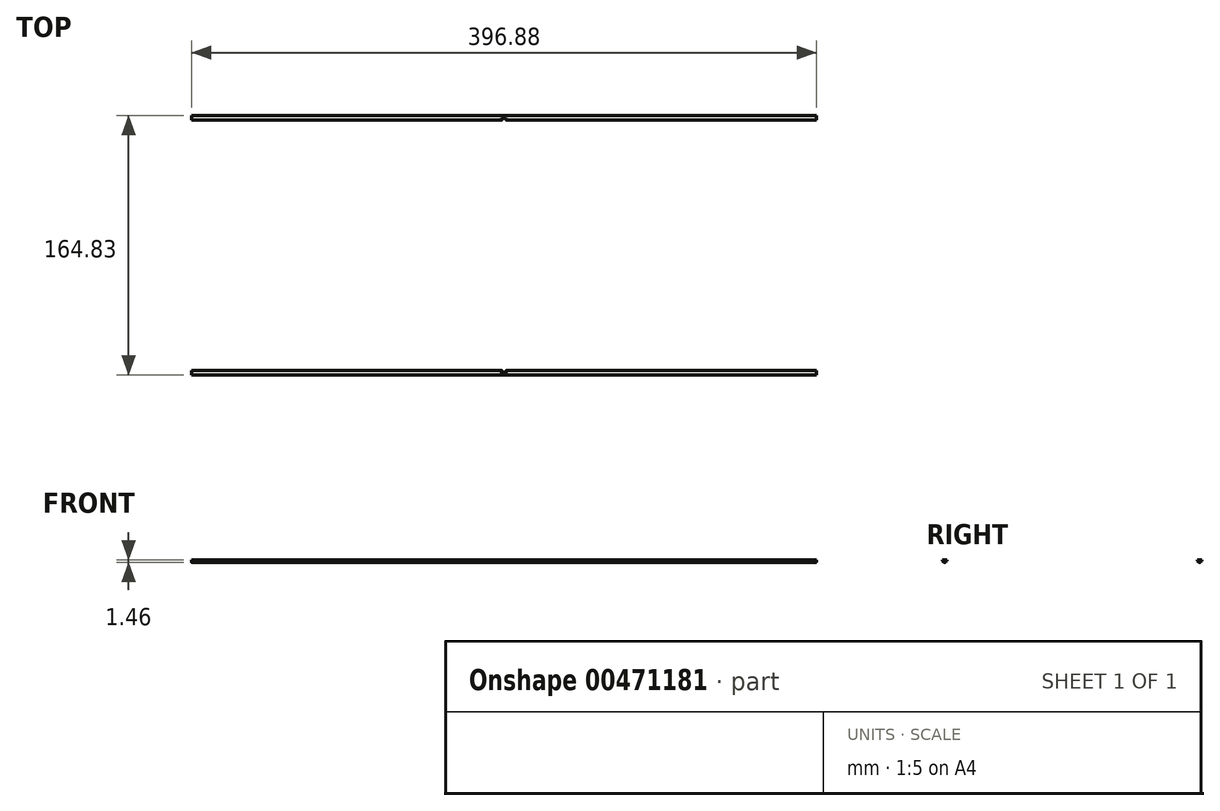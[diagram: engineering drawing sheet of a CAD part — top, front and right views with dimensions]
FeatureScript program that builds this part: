
annotation { "Feature Type Name" : "Feature", "Feature Type Description" : "" }
export const myFeature = defineFeature(function(context is Context, id is Id, definition is map)
    precondition{}
    {
        {
            var Q0;
            Q0=qCreatedBy(makeId("Top.planeOp"),FACE);
            var sketch = newSketch(context, id + "F0", { "sketchPlane" : qUnion([Q0])});
            skLineSegment(sketch, "E0", {"start": v(0, 0) * mm, "end": v(396.88, 0) * mm});
            skLineSegment(sketch, "E1", {"start": v(396.88, 0) * mm, "end": v(396.88, -193.68) * mm});
            skLineSegment(sketch, "E2", {"start": v(396.88, -193.68) * mm, "end": v(0, -193.68) * mm});
            skLineSegment(sketch, "E3", {"start": v(0, -193.68) * mm, "end": v(0, 0) * mm});
            skLineSegment(sketch, "E4.0", {"start": v(50.8, -31.75) * mm, "end": v(166.69, -31.75) * mm});
            skLineSegment(sketch, "E5.0", {"start": v(31.75, -142.88) * mm, "end": v(31.75, -50.8) * mm});
            skLineSegment(sketch, "E6.0", {"start": v(346.08, -161.93) * mm, "end": v(230.19, -161.93) * mm});
            skLineSegment(sketch, "E7.0", {"start": v(365.13, -50.8) * mm, "end": v(365.13, -142.88) * mm});
            skLineSegment(sketch, "E8.0", {"start": v(185.74, -142.88) * mm, "end": v(185.74, -50.8) * mm});
            skLineSegment(sketch, "E9.0", {"start": v(211.14, -142.88) * mm, "end": v(211.14, -50.8) * mm});
            skLineSegment(sketch, "E10.trimOffspring", {"start": v(230.19, -31.75) * mm, "end": v(346.08, -31.75) * mm});
            skLineSegment(sketch, "E11.trimOffspring", {"start": v(166.69, -161.93) * mm, "end": v(50.8, -161.93) * mm});
            skPoint(sketch, "E12.visualSharp", {"position": v(31.75, -31.75) * mm});
            skArc(sketch, "E12.filletArc", {"start": v(50.8, -31.75) * mm, "mid": v(37.33, -37.33) * mm, "end": v(31.75, -50.8) * mm});
            skPoint(sketch, "E13.visualSharp", {"position": v(31.75, -161.93) * mm});
            skArc(sketch, "E13.filletArc", {"start": v(31.75, -142.88) * mm, "mid": v(37.33, -156.35) * mm, "end": v(50.8, -161.93) * mm});
            skPoint(sketch, "E14.visualSharp", {"position": v(185.74, -31.75) * mm});
            skArc(sketch, "E14.filletArc", {"start": v(185.74, -50.8) * mm, "mid": v(180.16, -37.33) * mm, "end": v(166.69, -31.75) * mm});
            skPoint(sketch, "E15.visualSharp", {"position": v(185.74, -161.93) * mm});
            skArc(sketch, "E15.filletArc", {"start": v(166.69, -161.93) * mm, "mid": v(180.16, -156.35) * mm, "end": v(185.74, -142.88) * mm});
            skPoint(sketch, "E16.visualSharp", {"position": v(211.14, -161.93) * mm});
            skArc(sketch, "E16.filletArc", {"start": v(211.14, -142.88) * mm, "mid": v(216.72, -156.35) * mm, "end": v(230.19, -161.93) * mm});
            skPoint(sketch, "E17.visualSharp", {"position": v(211.14, -31.75) * mm});
            skArc(sketch, "E17.filletArc", {"start": v(230.19, -31.75) * mm, "mid": v(216.72, -37.33) * mm, "end": v(211.14, -50.8) * mm});
            skPoint(sketch, "E18.visualSharp", {"position": v(365.13, -31.75) * mm});
            skArc(sketch, "E18.filletArc", {"start": v(365.13, -50.8) * mm, "mid": v(359.55, -37.33) * mm, "end": v(346.08, -31.75) * mm});
            skPoint(sketch, "E19.visualSharp", {"position": v(365.13, -161.93) * mm});
            skArc(sketch, "E19.filletArc", {"start": v(346.08, -161.93) * mm, "mid": v(359.55, -156.35) * mm, "end": v(365.13, -142.88) * mm});
            skSolve(sketch);
        }
        {
            var Q0;
            Q0=makeQuery(id+"F0.imprint","IMPRINT",FACE,{"disambiguationData":[TD([[makeQuery(id+"F0.imprint","IMPRINT",EDGE,{"derivedFrom":sQuery(id+"F0.wireOp",EDGE,"E0")}),-1.0]])]});
            extrude(context, id + "F1", {"entities" : qUnion([Q0]), "depth" : 193.67 * mm});
        }
        {
            var Q0;
            Q0=makeQuery(id+"F1.opExtrude","SWEPT_FACE",FACE,{"disambiguationData":[OSD([sQuery(id+"F0.wireOp",EDGE,"E1")])]});
            var sketch = newSketch(context, id + "F2", { "sketchPlane" : qUnion([Q0])});
            skLineSegment(sketch, "E20", {"start": v(0, 0) * mm, "end": v(-15.88, 0) * mm});
            skCircle(sketch, "E21", {"center": v(-15.88, 0) * mm, "radius": 1.45 * mm});
            skLineSegment(sketch, "E22", {"start": v(-15.88, 0) * mm, "end": v(-177.8, 0) * mm});
            skLineSegment(sketch, "E23", {"start": v(-177.8, 0) * mm, "end": v(-193.68, 0) * mm});
            skCircle(sketch, "E24", {"center": v(-177.8, 0) * mm, "radius": 1.45 * mm});
            skLineSegment(sketch, "E25", {"start": v(0, 0) * mm, "end": v(0, 96.84) * mm});
            skLineSegment(sketch, "E26", {"start": v(0, 96.84) * mm, "end": v(-41.4, 96.84) * mm});
            skCircle(sketch, "E27.MirrorC", {"center": v(-15.88, 193.68) * mm, "radius": 1.45 * mm});
            skCircle(sketch, "E28.MirrorC", {"center": v(-177.8, 193.68) * mm, "radius": 1.45 * mm});
            skSolve(sketch);
        }
        {
            var Q0;
            {var subQ0=sQuery(id+"F2.wireOp",EDGE,"E28.MirrorC");var subQ1=makeQuery(id+"F1.opExtrude","CAP_EDGE",EDGE,{"disambiguationData":[OSD([sQuery(id+"F0.wireOp",EDGE,"E1")])],"isStart":false});var subQ2=makeQuery(id+"F2.imprint","INTERSECT",VERTEX,{"disambiguationData":[OD(0.0)],"derivedFrom":[subQ1,subQ0]});Q0=makeQuery(id+"F2.imprint","IMPRINT",FACE,{"disambiguationData":[TD([[makeQuery(id+"F2.imprint","IMPRINT",EDGE,{"disambiguationData":[TD([[subQ2,1.0]])],"derivedFrom":subQ0}),-1.0]])]});}
            var Q1;
            {var subQ0=sQuery(id+"F2.wireOp",EDGE,"E28.MirrorC");var subQ1=makeQuery(id+"F1.opExtrude","CAP_EDGE",EDGE,{"disambiguationData":[OSD([sQuery(id+"F0.wireOp",EDGE,"E1")])],"isStart":false});var subQ2=makeQuery(id+"F2.imprint","INTERSECT",VERTEX,{"disambiguationData":[OD(0.0)],"derivedFrom":[subQ1,subQ0]});Q1=makeQuery(id+"F2.imprint","IMPRINT",FACE,{"disambiguationData":[TD([[makeQuery(id+"F2.imprint","IMPRINT",EDGE,{"disambiguationData":[TD([[subQ2,-1.0]])],"derivedFrom":subQ0}),-1.0]])]});}
            var Q2;
            {var subQ0=sQuery(id+"F2.wireOp",EDGE,"E27.MirrorC");var subQ1=makeQuery(id+"F1.opExtrude","CAP_EDGE",EDGE,{"disambiguationData":[OSD([sQuery(id+"F0.wireOp",EDGE,"E1")])],"isStart":false});var subQ2=makeQuery(id+"F2.imprint","INTERSECT",VERTEX,{"disambiguationData":[OD(0.0)],"derivedFrom":[subQ1,subQ0]});Q2=makeQuery(id+"F2.imprint","IMPRINT",FACE,{"disambiguationData":[TD([[makeQuery(id+"F2.imprint","IMPRINT",EDGE,{"disambiguationData":[TD([[subQ2,1.0]])],"derivedFrom":subQ0}),-1.0]])]});}
            var Q3;
            {var subQ0=sQuery(id+"F2.wireOp",EDGE,"E27.MirrorC");var subQ1=makeQuery(id+"F1.opExtrude","CAP_EDGE",EDGE,{"disambiguationData":[OSD([sQuery(id+"F0.wireOp",EDGE,"E1")])],"isStart":false});var subQ2=makeQuery(id+"F2.imprint","INTERSECT",VERTEX,{"disambiguationData":[OD(0.0)],"derivedFrom":[subQ1,subQ0]});Q3=makeQuery(id+"F2.imprint","IMPRINT",FACE,{"disambiguationData":[TD([[makeQuery(id+"F2.imprint","IMPRINT",EDGE,{"disambiguationData":[TD([[subQ2,-1.0]])],"derivedFrom":subQ0}),-1.0]])]});}
            var Q4;
            {var subQ0=sQuery(id+"F2.wireOp",EDGE,"E22");var subQ1=sQuery(id+"F2.wireOp",EDGE,"E20");var subQ2=makeQuery(id+"F2.imprint","INTERSECT",VERTEX,{"derivedFrom":[subQ1,subQ0]});Q4=makeQuery(id+"F2.imprint","IMPRINT",FACE,{"disambiguationData":[TD([[makeQuery(id+"F2.imprint","IMPRINT",EDGE,{"disambiguationData":[TD([[subQ2,1.0]])],"derivedFrom":subQ1}),-1.0]])]});}
            var Q5;
            {var subQ0=sQuery(id+"F2.wireOp",EDGE,"E22");var subQ1=sQuery(id+"F2.wireOp",EDGE,"E20");var subQ2=makeQuery(id+"F2.imprint","INTERSECT",VERTEX,{"derivedFrom":[subQ1,subQ0]});Q5=makeQuery(id+"F2.imprint","IMPRINT",FACE,{"disambiguationData":[TD([[makeQuery(id+"F2.imprint","IMPRINT",EDGE,{"disambiguationData":[TD([[subQ2,1.0]])],"derivedFrom":subQ1}),1.0]])]});}
            var Q6;
            {var subQ0=sQuery(id+"F2.wireOp",EDGE,"E23");var subQ1=sQuery(id+"F2.wireOp",EDGE,"E22");var subQ2=makeQuery(id+"F2.imprint","INTERSECT",VERTEX,{"derivedFrom":[subQ1,subQ0]});Q6=makeQuery(id+"F2.imprint","IMPRINT",FACE,{"disambiguationData":[TD([[makeQuery(id+"F2.imprint","IMPRINT",EDGE,{"disambiguationData":[TD([[subQ2,1.0]])],"derivedFrom":subQ1}),-1.0]])]});}
            var Q7;
            {var subQ0=sQuery(id+"F2.wireOp",EDGE,"E23");var subQ1=sQuery(id+"F2.wireOp",EDGE,"E22");var subQ2=makeQuery(id+"F2.imprint","INTERSECT",VERTEX,{"derivedFrom":[subQ1,subQ0]});Q7=makeQuery(id+"F2.imprint","IMPRINT",FACE,{"disambiguationData":[TD([[makeQuery(id+"F2.imprint","IMPRINT",EDGE,{"disambiguationData":[TD([[subQ2,1.0]])],"derivedFrom":subQ1}),1.0]])]});}
            extrude(context, id + "F3", {"entities" : qUnion([Q0, Q1, Q2, Q3, Q4, Q5, Q6, Q7]), "operationType" : NewBodyOperationType.REMOVE, "oppositeDirection" : true, "depth" : 396.88 * mm});
        }
        {
            var Q0;
            Q0=qCreatedBy(makeId("Front.planeOp"),FACE);
            cPlane(context, id + "F4", {"entities" : qUnion([Q0]), "cplaneType" : CPlaneType.OFFSET, "offset" : 15.88 * mm, "width" : 152.4 * mm, "height" : 152.4 * mm});
        }
        {
            var Q0;
            Q0=qCreatedBy(id+"F4.planeOp",FACE);
            var sketch = newSketch(context, id + "F5", { "sketchPlane" : qUnion([Q0])});
            skLineSegment(sketch, "E29", {"start": v(0, 0) * mm, "end": v(0, 193.68) * mm});
            skLineSegment(sketch, "E30", {"start": v(0, 193.68) * mm, "end": v(198.44, 193.68) * mm});
            skCircle(sketch, "E31", {"center": v(198.44, 193.68) * mm, "radius": 1.45 * mm});
            skLineSegment(sketch, "E32", {"start": v(0, 96.84) * mm, "end": v(106.17, 96.84) * mm});
            skPoint(sketch, "E32.endSnap0", {"position": v(0, 96.84) * mm});
            skCircle(sketch, "E33.MirrorC", {"center": v(198.44, 0) * mm, "radius": 1.45 * mm});
            skSolve(sketch);
        }
        {
            var Q0;
            Q0=makeQuery(id+"F5.imprint","IMPRINT",FACE,{"disambiguationData":[TD([[makeQuery(id+"F5.imprint","IMPRINT",EDGE,{"derivedFrom":sQuery(id+"F5.wireOp",EDGE,"E31")}),1.0]])]});
            var Q1;
            Q1=makeQuery(id+"F5.imprint","IMPRINT",FACE,{"disambiguationData":[TD([[makeQuery(id+"F5.imprint","IMPRINT",EDGE,{"derivedFrom":sQuery(id+"F5.wireOp",EDGE,"E33.MirrorC")}),-1.0]])]});
            extrude(context, id + "F6", {"entities" : qUnion([Q0, Q1]), "operationType" : NewBodyOperationType.REMOVE, "depth" : 161.92 * mm});
        }
    });
